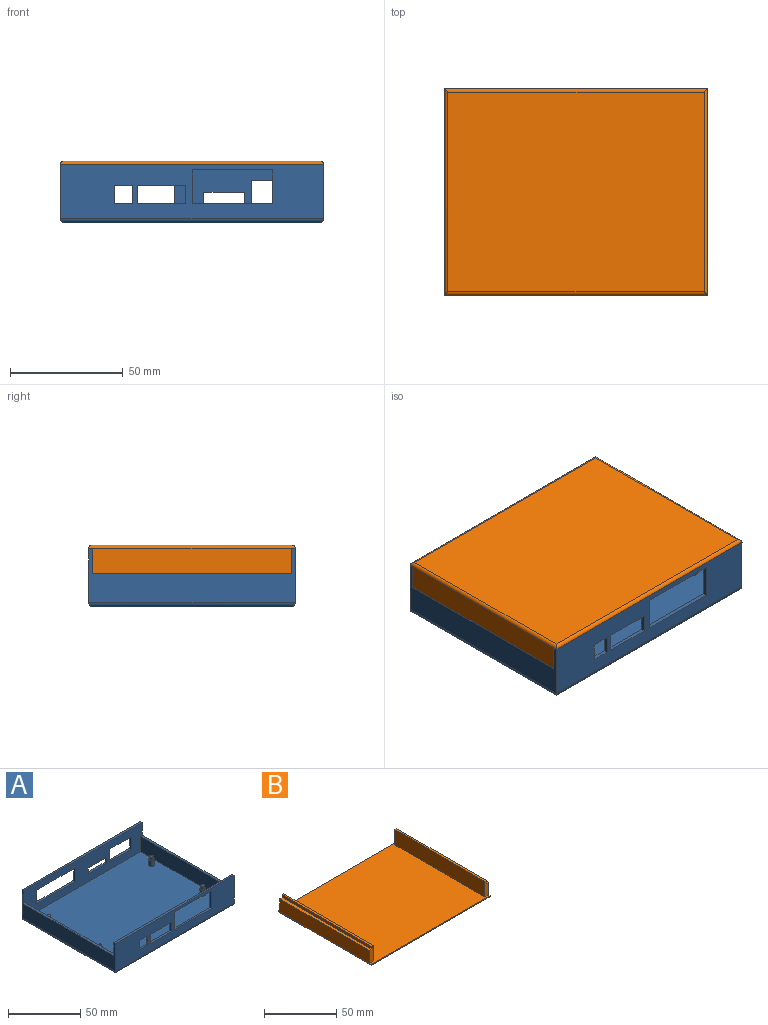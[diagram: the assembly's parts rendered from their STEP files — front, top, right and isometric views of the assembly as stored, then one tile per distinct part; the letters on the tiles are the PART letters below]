
ASSEMBLY  parts=2 mates=1
PART A: 58 faces, bbox 116.4x91.5x25.7 mm
  f0: plane 116.4x1.7mm, normal (0,0,1), area 197.9mm2, adj f1,f2,f3,f7
  f1: plane 91.5x23.7mm, normal (1,0,0), area 1199.5mm2, adj f0,f2,f3,f4,f5,f6,f55,f56
  f2: plane 116.4x23.7mm, normal (0,1,0), area 2011.2mm2, adj f0,f1,f7,f24,f25,f26,f27,f28
  f3: plane 116.4x24mm, normal (0,-1,0), area 2001.9mm2, adj f0,f1,f7,f9,f10,f11,f24,f25
  f4: plane 116.4x23.7mm, normal (0,-1,0), area 1991.2mm2, adj f1,f6,f7,f12,f13,f14,f15,f16
  f5: plane 116.4x24mm, normal (0,1,0), area 1981.9mm2, adj f1,f6,f7,f9,f10,f11,f12,f13
  f6: plane 116.4x1.7mm, normal (0,0,1), area 197.9mm2, adj f1,f4,f5,f7
  f7: plane 91.5x23.7mm, normal (-1,0,0), area 1199.4mm2, adj f0,f2,f3,f4,f5,f6,f52,f57
  f8: plane 112.4x87.5mm, normal (0,0,-1), area 9835mm2, adj f52,f53,f54,f55
  f9: plane 88.1x13mm, normal (1,0,0), area 1145.3mm2, adj f3,f5,f11,f57
  f10: plane 88.1x13mm, normal (-1,0,0), area 1145.3mm2, adj f3,f5,f11,f56
  f11: plane 113x88.1mm, normal (0,0,1), area 9905mm2, adj f3,f5,f9,f10,f36,f40,f44,f48
  f12: plane 15x1.7mm, normal (1,0,0), area 25.5mm2, adj f4,f5,f13,f15
  f13: plane 35.7x1.7mm, normal (0,0,1), area 60.7mm2, adj f4,f5,f12,f14
  f14: plane 15x1.7mm, normal (-1,0,0), area 25.5mm2, adj f4,f5,f13,f15
  f15: plane 35.7x1.7mm, normal (0,0,-1), area 60.7mm2, adj f4,f5,f12,f14
  f16: plane 21x1.7mm, normal (0,0,1), area 35.7mm2, adj f4,f5,f17,f19
  f17: plane 8x1.7mm, normal (-1,0,0), area 13.6mm2, adj f4,f5,f16,f18
  f18: plane 21x1.7mm, normal (0,0,-1), area 35.7mm2, adj f4,f5,f17,f19
  f19: plane 8x1.7mm, normal (1,0,0), area 13.6mm2, adj f4,f5,f16,f18
  f20: plane 8x1.7mm, normal (1,0,0), area 13.6mm2, adj f4,f5,f21,f23
  f21: plane 8x1.7mm, normal (0,0,1), area 13.6mm2, adj f4,f5,f20,f22
  f22: plane 8x1.7mm, normal (-1,0,0), area 13.6mm2, adj f4,f5,f21,f23
  f23: plane 8x1.7mm, normal (0,0,-1), area 13.6mm2, adj f4,f5,f20,f22
  f24: plane 21x1.7mm, normal (0,0,1), area 35.7mm2, adj f2,f3,f25,f27
  f25: plane 10.5x1.7mm, normal (1,0,0), area 17.9mm2, adj f2,f3,f24,f26
  f26: plane 21x1.7mm, normal (0,0,-1), area 35.7mm2, adj f2,f3,f25,f27
  f27: plane 10.5x1.7mm, normal (-1,0,0), area 17.9mm2, adj f2,f3,f24,f26
  f28: plane 5x1.7mm, normal (-1,0,0), area 8.5mm2, adj f2,f3,f29,f31
  f29: plane 18x1.7mm, normal (0,0,1), area 30.6mm2, adj f2,f3,f28,f30
  f30: plane 5x1.7mm, normal (1,0,0), area 8.5mm2, adj f2,f3,f29,f31
  f31: plane 18x1.7mm, normal (0,0,-1), area 30.6mm2, adj f2,f3,f28,f30
  f32: plane 38x1.7mm, normal (0,0,1), area 64.6mm2, adj f2,f3,f33,f35
  f33: plane 11.5x1.7mm, normal (1,0,0), area 19.6mm2, adj f2,f3,f32,f34
  f34: plane 38x1.7mm, normal (0,0,-1), area 64.6mm2, adj f2,f3,f33,f35
  f35: plane 11.5x1.7mm, normal (-1,0,0), area 19.6mm2, adj f2,f3,f32,f34
  f36: cylinder r=2mm len=5mm, axis (0,0,-1), area 62.8mm2, adj f11,f37
  f37: plane 4x4mm, normal (0,0,1), area 7.7mm2, adj f36,f39
  f38: plane 2.5x2.5mm, normal (0,0,1), area 4.9mm2, adj f39
  f39: cylinder r=1.25mm len=2.5mm, axis (0,0,-1), area 19.6mm2, adj f37,f38
  f40: cylinder r=2mm len=5mm, axis (0,0,-1), area 62.8mm2, adj f11,f41
  f41: plane 4x4mm, normal (0,0,1), area 7.7mm2, adj f40,f43
  f42: plane 2.5x2.5mm, normal (0,0,1), area 4.9mm2, adj f43
  f43: cylinder r=1.25mm len=2.5mm, axis (0,0,-1), area 19.6mm2, adj f41,f42
  f44: cylinder r=2mm len=5mm, axis (0,0,-1), area 62.8mm2, adj f11,f45
  f45: plane 4x4mm, normal (0,0,1), area 7.7mm2, adj f44,f47
  f46: plane 2.5x2.5mm, normal (0,0,1), area 4.9mm2, adj f47
  f47: cylinder r=1.25mm len=2.5mm, axis (0,0,-1), area 19.6mm2, adj f45,f46
  f48: cylinder r=2mm len=5mm, axis (0,0,-1), area 62.8mm2, adj f11,f49
  f49: plane 4x4mm, normal (0,0,1), area 7.7mm2, adj f48,f51
  f50: plane 2.5x2.5mm, normal (0,0,1), area 4.9mm2, adj f51
  f51: cylinder r=1.25mm len=2.5mm, axis (0,0,-1), area 19.6mm2, adj f49,f50
  f52: cylinder r=2mm len=91.5mm, axis (0,-1,0), area 282.9mm2, adj f7,f8,f53,f54
  f53: cylinder r=2mm len=116.4mm, axis (1,0,0), area 361.1mm2, adj f4,f8,f52,f55
  f54: cylinder r=2mm len=116.4mm, axis (-1,0,0), area 361.1mm2, adj f2,f8,f52,f55
  f55: cylinder r=2mm len=91.5mm, axis (0,1,0), area 282.9mm2, adj f1,f8,f53,f54
  f56: plane 88.1x1.7mm, normal (0,0,1), area 149.8mm2, adj f1,f3,f5,f10
  f57: plane 88.1x1.7mm, normal (0,0,1), area 149.8mm2, adj f3,f5,f7,f9
PART B: 22 faces, bbox 116.4x91.5x14.7 mm
  f0: plane 116.4x91.5mm, normal (0,0,1), area 9989.8mm2, adj f1,f2,f3,f4,f6,f7,f9,f10
  f1: plane 91.5x11mm, normal (1,0,0), area 969.8mm2, adj f0,f2,f4,f9,f10,f11,f12
  f2: plane 116.4x0.2mm, normal (0,1,0), area 23.3mm2, adj f0,f1,f3,f13
  f3: plane 91.5x11mm, normal (-1,0,0), area 969.8mm2, adj f0,f2,f4,f6,f7,f8,f15
  f4: plane 116.4x0.2mm, normal (0,-1,0), area 23.3mm2, adj f0,f1,f3,f14
  f5: plane 113.4x88.5mm, normal (0,0,-1), area 10035.9mm2, adj f12,f13,f14,f15
  f6: plane 13x4.1mm, normal (0,-1,0), area 48mm2, adj f0,f3,f8,f16,f17,f18
  f7: plane 13x4.1mm, normal (0,1,0), area 48mm2, adj f0,f3,f8,f16,f17,f18
  f8: plane 88.1x2.4mm, normal (0,0,1), area 211.4mm2, adj f3,f6,f7,f16
  f9: plane 13x3.4mm, normal (0,-1,0), area 40.5mm2, adj f0,f1,f11,f19,f20,f21
  f10: plane 13x3.4mm, normal (0,1,0), area 40.5mm2, adj f0,f1,f11,f19,f20,f21
  f11: plane 88.1x1.7mm, normal (0,0,1), area 149.8mm2, adj f1,f9,f10,f19
  f12: cylinder r=1.5mm len=91.5mm, axis (0,1,0), area 213mm2, adj f1,f5,f13,f14
  f13: cylinder r=1.5mm len=116.4mm, axis (-1,0,0), area 271.7mm2, adj f2,f5,f12,f15
  f14: cylinder r=1.5mm len=116.4mm, axis (1,0,0), area 271.7mm2, adj f4,f5,f12,f15
  f15: cylinder r=1.5mm len=91.5mm, axis (0,-1,0), area 213mm2, adj f3,f5,f13,f14
  f16: plane 88.1x2.2mm, normal (-1,0,0), area 193.8mm2, adj f6,f7,f8,f18
  f17: plane 88.1x13mm, normal (1,0,0), area 1145.3mm2, adj f0,f6,f7,f18
  f18: plane 88.1x1.7mm, normal (0,0,1), area 149.8mm2, adj f6,f7,f16,f17
  f19: plane 88.1x2.2mm, normal (1,0,0), area 193.8mm2, adj f9,f10,f11,f21
  f20: plane 88.1x13mm, normal (-1,0,0), area 1145.3mm2, adj f0,f9,f10,f21
  f21: plane 88.1x1.7mm, normal (0,0,1), area 149.8mm2, adj f9,f10,f19,f20
PLACE A at identity fixed
PLACE B rot(axis=(1,0,0),180deg) t=(0,-15.49,25.7)mm
MATE slider B.f0 <-> A.f6  axis (0,0,-1) through (-1.7,-1.7,24)mm
